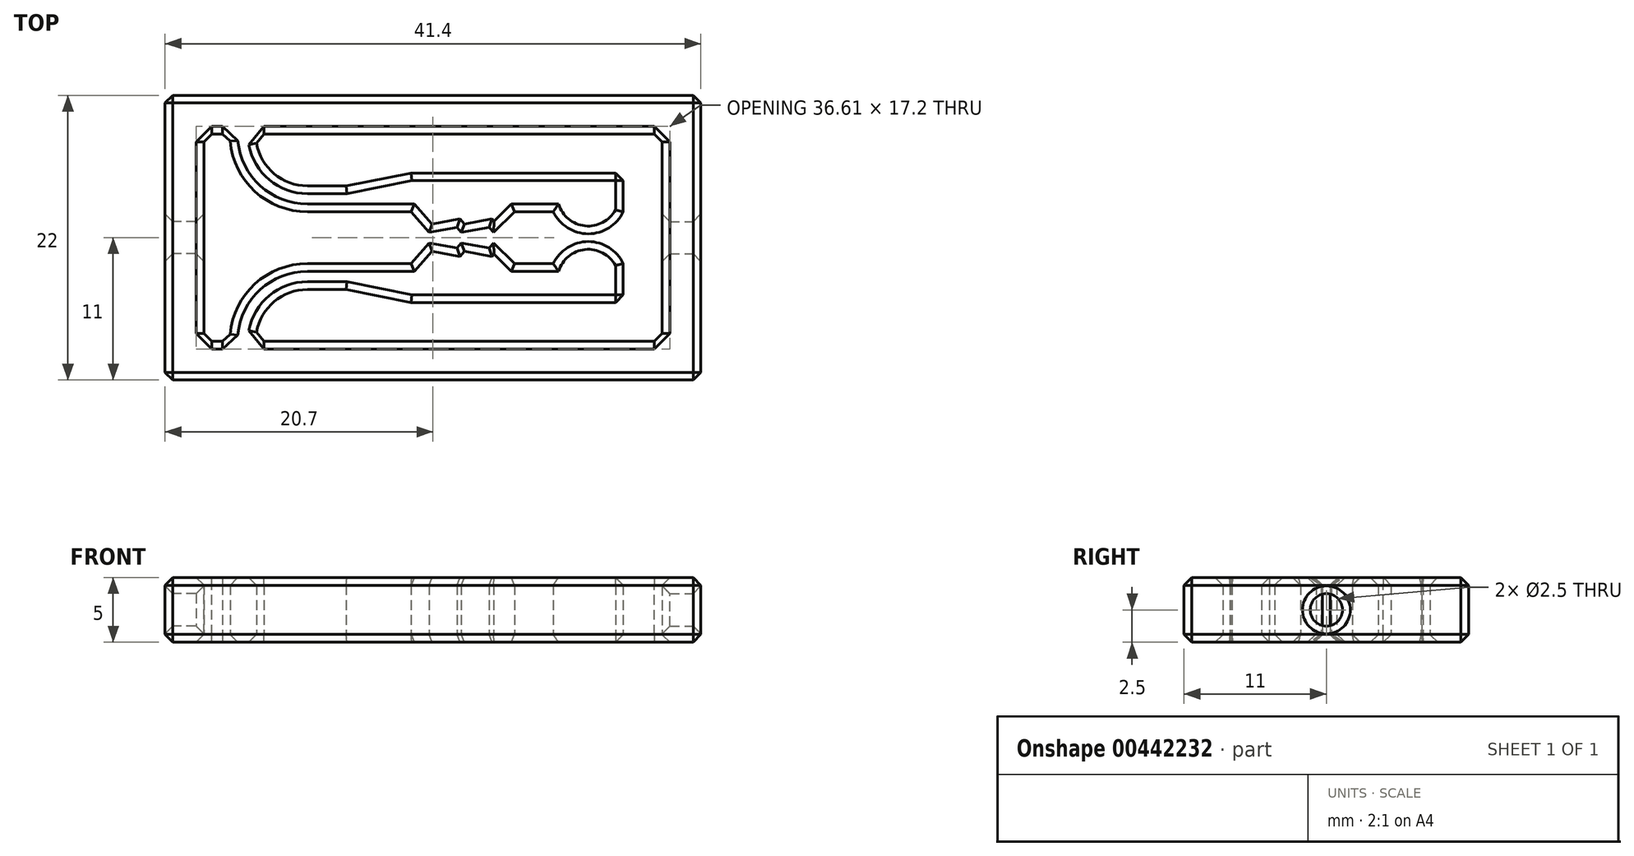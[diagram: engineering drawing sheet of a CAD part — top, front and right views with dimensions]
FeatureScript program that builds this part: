
annotation { "Feature Type Name" : "Feature", "Feature Type Description" : "" }
export const myFeature = defineFeature(function(context is Context, id is Id, definition is map)
    precondition{}
    {
        {
            var Q0;
            Q0=qCreatedBy(makeId("Top.planeOp"),FACE);
            var sketch = newSketch(context, id + "F0", { "sketchPlane" : qUnion([Q0])});
            skLineSegment(sketch, "E0", {"start": v(-13.7, -2) * mm, "end": v(-12.3, -0.4) * mm});
            skLineSegment(sketch, "E1", {"start": v(-12.3, -0.4) * mm, "end": v(-10.15, -0.8) * mm});
            skLineSegment(sketch, "E2", {"start": v(-10.15, -0.8) * mm, "end": v(-9.8, -0.4) * mm});
            skLineSegment(sketch, "E3", {"start": v(-9.8, -0.4) * mm, "end": v(-7.65, -0.8) * mm});
            skLineSegment(sketch, "E4", {"start": v(-7.65, -0.8) * mm, "end": v(-7.3, -0.4) * mm});
            skLineSegment(sketch, "E5", {"start": v(-7.3, -0.4) * mm, "end": v(-5.7, -2) * mm});
            skLineSegment(sketch, "E6", {"start": v(-5.7, -2) * mm, "end": v(-2.7, -2) * mm});
            skLineSegment(sketch, "E7", {"start": v(-2.7, -2) * mm, "end": v(2.7, -2) * mm, "construction": true});
            skLineSegment(sketch, "E8", {"start": v(2.7, -2) * mm, "end": v(2.7, -5) * mm});
            skLineSegment(sketch, "E9", {"start": v(2.7, -5) * mm, "end": v(-13.7, -5) * mm});
            skLineSegment(sketch, "E10", {"start": v(-13.7, -5) * mm, "end": v(-18.7, -4) * mm});
            skArc(sketch, "E11", {"start": v(-2.7, -2) * mm, "mid": v(0, -0.3) * mm, "end": v(2.7, -2) * mm});
            skLineSegment(sketch, "E12", {"start": v(-13.7, -2) * mm, "end": v(-5.7, -2) * mm, "construction": true});
            skLineSegment(sketch, "E13", {"start": v(-13.7, -2) * mm, "end": v(-21.7, -2) * mm});
            skLineSegment(sketch, "E14", {"start": v(-18.7, -4) * mm, "end": v(-21.7, -4) * mm});
            skArc(sketch, "E15", {"start": v(-21.7, -4) * mm, "mid": v(-24.53, -5.17) * mm, "end": v(-25.7, -8) * mm});
            skArc(sketch, "E16", {"start": v(-21.7, -2) * mm, "mid": v(-25.95, -3.76) * mm, "end": v(-27.7, -8) * mm});
            skLineSegment(sketch, "E17", {"start": v(-25.7, -8) * mm, "end": v(5.7, -8) * mm});
            skLineSegment(sketch, "E18", {"start": v(8.7, 11) * mm, "end": v(8.7, -11) * mm});
            skLineSegment(sketch, "E19", {"start": v(8.7, -11) * mm, "end": v(-32.7, -11) * mm});
            skLineSegment(sketch, "E20", {"start": v(-32.7, -11) * mm, "end": v(-32.7, 11) * mm});
            skLineSegment(sketch, "E21", {"start": v(-29.7, 8) * mm, "end": v(-29.7, -8) * mm});
            skLineSegment(sketch, "E22", {"start": v(-29.7, -8) * mm, "end": v(-27.7, -8) * mm});
            skLineSegment(sketch, "E23", {"start": v(5.7, -8) * mm, "end": v(5.7, 8) * mm});
            skLineSegment(sketch, "E24", {"start": v(-29.7, -8) * mm, "end": v(-32.7, -8) * mm, "construction": true});
            skLineSegment(sketch, "E25", {"start": v(5.7, -8) * mm, "end": v(8.7, -8) * mm, "construction": true});
            skLineSegment(sketch, "E26", {"start": v(-29.7, -8) * mm, "end": v(-29.7, -11) * mm, "construction": true});
            skLineSegment(sketch, "E27.MirrorCS", {"start": v(-7.3, 0.4) * mm, "end": v(-5.7, 2) * mm});
            skLineSegment(sketch, "E28.MirrorCS", {"start": v(-29.7, 8) * mm, "end": v(-27.7, 8) * mm});
            skLineSegment(sketch, "E29.MirrorCS", {"start": v(-7.65, 0.8) * mm, "end": v(-7.3, 0.4) * mm});
            skLineSegment(sketch, "E30.MirrorCS", {"start": v(-2.7, 2) * mm, "end": v(2.7, 2) * mm, "construction": true});
            skLineSegment(sketch, "E31.MirrorCS", {"start": v(-13.7, 2) * mm, "end": v(-5.7, 2) * mm, "construction": true});
            skArc(sketch, "E32.MirrorCS", {"start": v(-2.7, 2) * mm, "mid": v(0, 0.3) * mm, "end": v(2.7, 2) * mm});
            skArc(sketch, "E33.MirrorCS", {"start": v(-21.7, 2) * mm, "mid": v(-25.95, 3.76) * mm, "end": v(-27.7, 8) * mm});
            skLineSegment(sketch, "E34.MirrorCS", {"start": v(-5.7, 2) * mm, "end": v(-2.7, 2) * mm});
            skLineSegment(sketch, "E35.MirrorCS", {"start": v(-9.8, 0.4) * mm, "end": v(-7.65, 0.8) * mm});
            skLineSegment(sketch, "E36.MirrorCS", {"start": v(2.7, 5) * mm, "end": v(-13.7, 5) * mm});
            skLineSegment(sketch, "E37.MirrorCS", {"start": v(8.7, 11) * mm, "end": v(-32.7, 11) * mm});
            skLineSegment(sketch, "E38.MirrorCS", {"start": v(2.7, 2) * mm, "end": v(2.7, 5) * mm});
            skLineSegment(sketch, "E39.MirrorCS", {"start": v(-12.3, 0.4) * mm, "end": v(-10.15, 0.8) * mm});
            skLineSegment(sketch, "E40.MirrorCS", {"start": v(-13.7, 2) * mm, "end": v(-12.3, 0.4) * mm});
            skLineSegment(sketch, "E41.MirrorCS", {"start": v(-25.7, 8) * mm, "end": v(5.7, 8) * mm});
            skLineSegment(sketch, "E42.MirrorCS", {"start": v(-13.7, 5) * mm, "end": v(-18.7, 4) * mm});
            skLineSegment(sketch, "E43.MirrorCS", {"start": v(-18.7, 4) * mm, "end": v(-21.7, 4) * mm});
            skArc(sketch, "E44.MirrorCS", {"start": v(-21.7, 4) * mm, "mid": v(-24.53, 5.17) * mm, "end": v(-25.7, 8) * mm});
            skLineSegment(sketch, "E45.MirrorCS", {"start": v(-13.7, 2) * mm, "end": v(-21.7, 2) * mm});
            skLineSegment(sketch, "E46.MirrorCS", {"start": v(-10.15, 0.8) * mm, "end": v(-9.8, 0.4) * mm});
            skLineSegment(sketch, "E47", {"start": v(-12.3, -0.4) * mm, "end": v(-7.3, -0.4) * mm, "construction": true});
            skSolve(sketch);
        }
        {
            var Q0;
            Q0 = qSketchRegion(id + "F0", true);
            extrude(context, id + "F1", {"entities" : qUnion([Q0]), "endBound" : BoundingType.SYMMETRIC, "depth" : 5 * mm});
        }
        {
            var Q0;
            Q0=makeQuery(id+"F1.opExtrude","SWEPT_FACE",FACE,{"disambiguationData":[OSD([sQuery(id+"F0.wireOp",EDGE,"E20")])]});
            var sketch = newSketch(context, id + "F2", { "sketchPlane" : qUnion([Q0])});
            skCircle(sketch, "E48", {"center": v(0, 0) * mm, "radius": 1.25 * mm});
            skSolve(sketch);
        }
        {
            var Q0;
            Q0 = qSketchRegion(id + "F2", true);
            extrude(context, id + "F3", {"entities" : qUnion([Q0]), "operationType" : NewBodyOperationType.REMOVE, "endBound" : BoundingType.UP_TO_NEXT, "oppositeDirection" : true, "depth" : 25 * mm});
        }
        {
            var Q0;
            Q0=makeQuery(id+"F1.opExtrude","SWEPT_FACE",FACE,{"disambiguationData":[OSD([sQuery(id+"F0.wireOp",EDGE,"E18")])]});
            var sketch = newSketch(context, id + "F4", { "sketchPlane" : qUnion([Q0])});
            skCircle(sketch, "E49", {"center": v(0, 0) * mm, "radius": 1.25 * mm});
            skSolve(sketch);
        }
        {
            var Q0;
            Q0 = qSketchRegion(id + "F4", true);
            extrude(context, id + "F5", {"entities" : qUnion([Q0]), "operationType" : NewBodyOperationType.REMOVE, "endBound" : BoundingType.UP_TO_NEXT, "oppositeDirection" : true, "depth" : 25 * mm});
        }
        {
            var Q0;
            Q0=makeQuery(id+"F1.opExtrude","CAP_FACE",FACE,{"disambiguationData":[OSD([sQuery(id+"F0.wireOp",EDGE,"E0"),sQuery(id+"F0.wireOp",EDGE,"E1"),sQuery(id+"F0.wireOp",EDGE,"E2"),sQuery(id+"F0.wireOp",EDGE,"E3"),sQuery(id+"F0.wireOp",EDGE,"E4"),sQuery(id+"F0.wireOp",EDGE,"E5"),sQuery(id+"F0.wireOp",EDGE,"E6"),sQuery(id+"F0.wireOp",EDGE,"E8"),sQuery(id+"F0.wireOp",EDGE,"E9"),sQuery(id+"F0.wireOp",EDGE,"E10"),sQuery(id+"F0.wireOp",EDGE,"E11"),sQuery(id+"F0.wireOp",EDGE,"E13"),sQuery(id+"F0.wireOp",EDGE,"E14"),sQuery(id+"F0.wireOp",EDGE,"E15"),sQuery(id+"F0.wireOp",EDGE,"E16"),sQuery(id+"F0.wireOp",EDGE,"E17"),sQuery(id+"F0.wireOp",EDGE,"E18"),sQuery(id+"F0.wireOp",EDGE,"E19"),sQuery(id+"F0.wireOp",EDGE,"E20"),sQuery(id+"F0.wireOp",EDGE,"E21"),sQuery(id+"F0.wireOp",EDGE,"E22"),sQuery(id+"F0.wireOp",EDGE,"E23"),sQuery(id+"F0.wireOp",EDGE,"E27.MirrorCS"),sQuery(id+"F0.wireOp",EDGE,"E28.MirrorCS"),sQuery(id+"F0.wireOp",EDGE,"E29.MirrorCS"),sQuery(id+"F0.wireOp",EDGE,"E32.MirrorCS"),sQuery(id+"F0.wireOp",EDGE,"E33.MirrorCS"),sQuery(id+"F0.wireOp",EDGE,"E34.MirrorCS"),sQuery(id+"F0.wireOp",EDGE,"E35.MirrorCS"),sQuery(id+"F0.wireOp",EDGE,"E36.MirrorCS"),sQuery(id+"F0.wireOp",EDGE,"E37.MirrorCS"),sQuery(id+"F0.wireOp",EDGE,"E38.MirrorCS"),sQuery(id+"F0.wireOp",EDGE,"E39.MirrorCS"),sQuery(id+"F0.wireOp",EDGE,"E40.MirrorCS"),sQuery(id+"F0.wireOp",EDGE,"E41.MirrorCS"),sQuery(id+"F0.wireOp",EDGE,"E42.MirrorCS"),sQuery(id+"F0.wireOp",EDGE,"E43.MirrorCS"),sQuery(id+"F0.wireOp",EDGE,"E44.MirrorCS"),sQuery(id+"F0.wireOp",EDGE,"E45.MirrorCS"),sQuery(id+"F0.wireOp",EDGE,"E46.MirrorCS")])],"isStart":false});
            var Q1;
            Q1=makeQuery(id+"F1.opExtrude","CAP_FACE",FACE,{"disambiguationData":[OSD([sQuery(id+"F0.wireOp",EDGE,"E0"),sQuery(id+"F0.wireOp",EDGE,"E1"),sQuery(id+"F0.wireOp",EDGE,"E2"),sQuery(id+"F0.wireOp",EDGE,"E3"),sQuery(id+"F0.wireOp",EDGE,"E4"),sQuery(id+"F0.wireOp",EDGE,"E5"),sQuery(id+"F0.wireOp",EDGE,"E6"),sQuery(id+"F0.wireOp",EDGE,"E8"),sQuery(id+"F0.wireOp",EDGE,"E9"),sQuery(id+"F0.wireOp",EDGE,"E10"),sQuery(id+"F0.wireOp",EDGE,"E11"),sQuery(id+"F0.wireOp",EDGE,"E13"),sQuery(id+"F0.wireOp",EDGE,"E14"),sQuery(id+"F0.wireOp",EDGE,"E15"),sQuery(id+"F0.wireOp",EDGE,"E16"),sQuery(id+"F0.wireOp",EDGE,"E17"),sQuery(id+"F0.wireOp",EDGE,"E18"),sQuery(id+"F0.wireOp",EDGE,"E19"),sQuery(id+"F0.wireOp",EDGE,"E20"),sQuery(id+"F0.wireOp",EDGE,"E21"),sQuery(id+"F0.wireOp",EDGE,"E22"),sQuery(id+"F0.wireOp",EDGE,"E23"),sQuery(id+"F0.wireOp",EDGE,"E27.MirrorCS"),sQuery(id+"F0.wireOp",EDGE,"E28.MirrorCS"),sQuery(id+"F0.wireOp",EDGE,"E29.MirrorCS"),sQuery(id+"F0.wireOp",EDGE,"E32.MirrorCS"),sQuery(id+"F0.wireOp",EDGE,"E33.MirrorCS"),sQuery(id+"F0.wireOp",EDGE,"E34.MirrorCS"),sQuery(id+"F0.wireOp",EDGE,"E35.MirrorCS"),sQuery(id+"F0.wireOp",EDGE,"E36.MirrorCS"),sQuery(id+"F0.wireOp",EDGE,"E37.MirrorCS"),sQuery(id+"F0.wireOp",EDGE,"E38.MirrorCS"),sQuery(id+"F0.wireOp",EDGE,"E39.MirrorCS"),sQuery(id+"F0.wireOp",EDGE,"E40.MirrorCS"),sQuery(id+"F0.wireOp",EDGE,"E41.MirrorCS"),sQuery(id+"F0.wireOp",EDGE,"E42.MirrorCS"),sQuery(id+"F0.wireOp",EDGE,"E43.MirrorCS"),sQuery(id+"F0.wireOp",EDGE,"E44.MirrorCS"),sQuery(id+"F0.wireOp",EDGE,"E45.MirrorCS"),sQuery(id+"F0.wireOp",EDGE,"E46.MirrorCS")])],"isStart":true});
            var Q2;
            Q2=makeQuery(id+"F1.opExtrude","SWEPT_FACE",FACE,{"disambiguationData":[OSD([sQuery(id+"F0.wireOp",EDGE,"E20")])]});
            var Q3;
            Q3=makeQuery(id+"F1.opExtrude","SWEPT_FACE",FACE,{"disambiguationData":[OSD([sQuery(id+"F0.wireOp",EDGE,"E18")])]});
            var Q4;
            Q4=makeQuery(id+"F1.opExtrude","SWEPT_FACE",FACE,{"disambiguationData":[OSD([sQuery(id+"F0.wireOp",EDGE,"E21")])]});
            var Q5;
            Q5=makeQuery(id+"F1.opExtrude","SWEPT_FACE",FACE,{"disambiguationData":[OSD([sQuery(id+"F0.wireOp",EDGE,"E23")])]});
            var Q6;
            Q6=makeQuery(id+"F1.opExtrude","SWEPT_FACE",FACE,{"disambiguationData":[OSD([sQuery(id+"F0.wireOp",EDGE,"E17")])]});
            var Q7;
            Q7=makeQuery(id+"F1.opExtrude","SWEPT_FACE",FACE,{"disambiguationData":[OSD([sQuery(id+"F0.wireOp",EDGE,"E22")])]});
            var Q8;
            Q8=makeQuery(id+"F1.opExtrude","SWEPT_FACE",FACE,{"disambiguationData":[OSD([sQuery(id+"F0.wireOp",EDGE,"E41.MirrorCS")])]});
            var Q9;
            Q9=makeQuery(id+"F1.opExtrude","SWEPT_FACE",FACE,{"disambiguationData":[OSD([sQuery(id+"F0.wireOp",EDGE,"E28.MirrorCS")])]});
            var Q10;
            Q10=makeQuery(id+"F1.opExtrude","SWEPT_EDGE",EDGE,{"disambiguationData":[OSD([sQuery(id+"F0.wireOp",EDGE,"E36.MirrorCS"),sQuery(id+"F0.wireOp",EDGE,"E38.MirrorCS")])]});
            var Q11;
            Q11=makeQuery(id+"F1.opExtrude","SWEPT_EDGE",EDGE,{"disambiguationData":[OSD([sQuery(id+"F0.wireOp",EDGE,"E8"),sQuery(id+"F0.wireOp",EDGE,"E9")])]});
            chamfer(context, id + "F6", {"entities" : qUnion([Q0, Q1, Q2, Q3, Q4, Q5, Q6, Q7, Q8, Q9, Q10, Q11]), "width" : 0.6 * mm, "tangentPropagation" : true});
        }
    });
